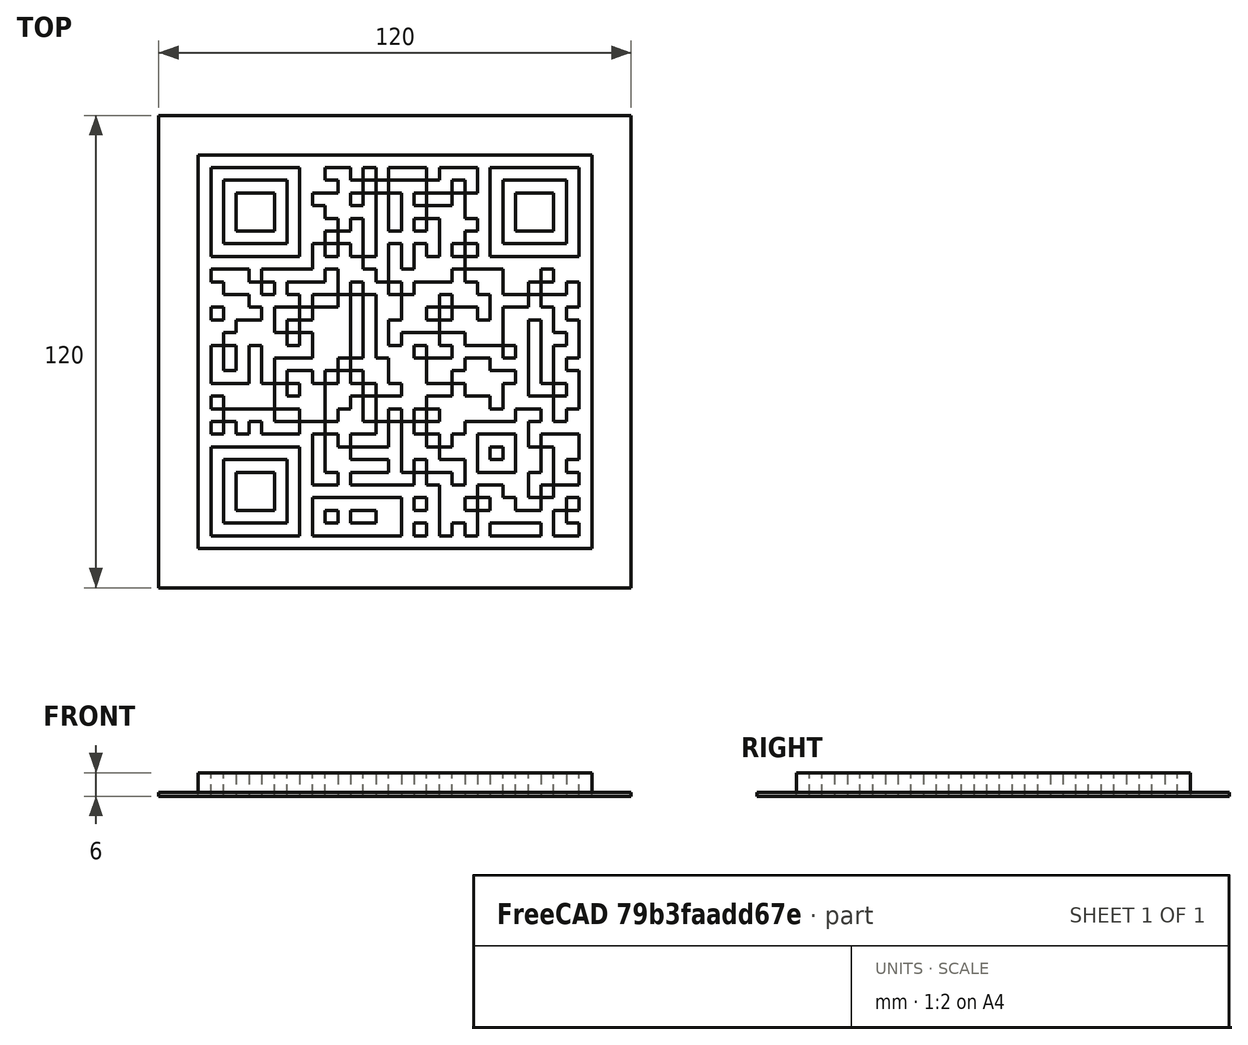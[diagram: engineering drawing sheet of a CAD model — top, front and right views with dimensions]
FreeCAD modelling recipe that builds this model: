
FCSTD DOCUMENT  (FreeCAD 1.0R)
Label: 未命名
License: All rights reserved
objects: Part::Feature×2, Mesh::Feature×2, Sketcher::SketchObject×1, PartDesign::Pad×1, PartDesign::Body×1
note: 8 computed .brp shape members not serialized (recipe doc carries the construction recipe); baked Part::Feature solids carry a one-line shape summary decoded from their .brp

FEATURE [Part::Feature] _____________________001_solid  label="_____________________001 (Solid)"
  shape: bbox 100 x 100 x 6 mm, 4116 faces (baked)
FEATURE [Part::Feature] _____________________001
  shape: bbox 100 x 100 x 6 mm, 4116 faces, 0 solids (baked)
FEATURE [Mesh::Feature] _____________________  label="教室门口展示牌"
FEATURE [Sketcher::SketchObject] Sketch
  ArcFitTolerance = 1e-06
  AttachmentSupport = -> [XY_Plane]
  FullyConstrained = true
  MakeInternals = false
  MapMode = 5
  sketch-geometry (5):
    g0: LineSegment StartX=-60 StartY=-60 StartZ=0 EndX=60 EndY=-60 EndZ=0
    g1: LineSegment StartX=60 StartY=-60 StartZ=0 EndX=60 EndY=60 EndZ=0
    g2: LineSegment StartX=60 StartY=60 StartZ=0 EndX=-60 EndY=60 EndZ=0
    g3: LineSegment StartX=-60 StartY=60 StartZ=0 EndX=-60 EndY=-60 EndZ=0
    g4: GeomPoint [constr] X=0 Y=0 Z=0
  constraints (12):
    c: Coincident(g0,g1)
    c: Coincident(g1,g2)
    c: Coincident(g2,g3)
    c: Coincident(g3,g0)
    c: Horizontal(g0)
    c: Horizontal(g2)
    c: Vertical(g1)
    c: Vertical(g3)
    c: Symmetric(g2,g0,g4)
    c: Distance(g1,g3) = 120
    c: Distance(g0,g2) = 120
    c: Coincident(g4,g-1)
FEATURE [PartDesign::Pad] Pad
  Direction = (0,0,1)
  Length = 1
  Length2 = 10
  Profile = -> Sketch
  ReferenceAxis = -> Sketch [N_Axis]
  Refine = true
  Suppressed = false
  Type = 0
FEATURE [PartDesign::Body] Body
  AllowCompound = false
  Group = -> [Sketch,Pad]
  Origin = -> Origin
  Tip = -> Pad
FEATURE [Mesh::Feature] _____________________002  label="教室门口展示牌001"
